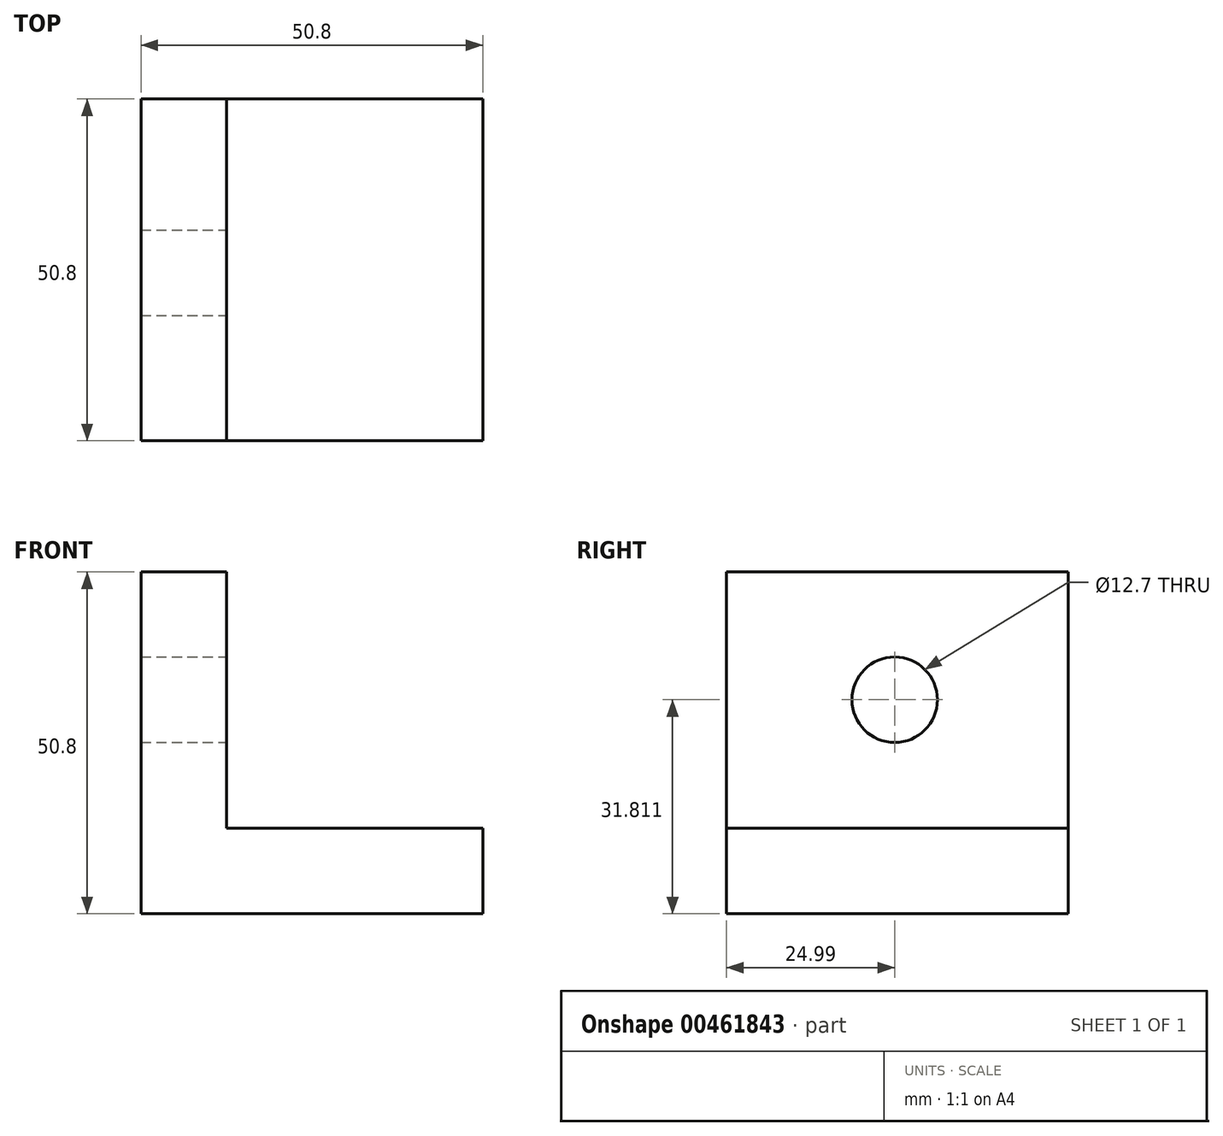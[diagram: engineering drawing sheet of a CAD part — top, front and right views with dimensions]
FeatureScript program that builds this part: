
annotation { "Feature Type Name" : "Feature", "Feature Type Description" : "" }
export const myFeature = defineFeature(function(context is Context, id is Id, definition is map)
    precondition{}
    {
        {
            var Q0;
            Q0=qCreatedBy(makeId("Front.planeOp"),FACE);
            var sketch = newSketch(context, id + "F0", { "sketchPlane" : qUnion([Q0])});
            skLineSegment(sketch, "E0.bottom", {"start": v(-27.84, 30.46) * mm, "end": v(22.96, 30.46) * mm});
            skLineSegment(sketch, "E0.top", {"start": v(-27.84, -20.34) * mm, "end": v(22.96, -20.34) * mm});
            skLineSegment(sketch, "E0.left", {"start": v(-27.84, 30.46) * mm, "end": v(-27.84, -20.34) * mm});
            skLineSegment(sketch, "E0.right", {"start": v(22.96, 30.46) * mm, "end": v(22.96, -20.34) * mm});
            skSolve(sketch);
        }
        {
            var Q0;
            Q0=makeQuery(id+"F0.imprint","IMPRINT",FACE,{"disambiguationData":[TD([[makeQuery(id+"F0.imprint","IMPRINT",EDGE,{"derivedFrom":sQuery(id+"F0.wireOp",EDGE,"E0.bottom")}),-1.0]])]});
            extrude(context, id + "F1", {"entities" : qUnion([Q0]), "depth" : 50.8 * mm});
        }
        {
            var Q0;
            Q0=makeQuery(id+"F1.opExtrude","CAP_FACE",FACE,{"disambiguationData":[OSD([sQuery(id+"F0.wireOp",EDGE,"E0.bottom"),sQuery(id+"F0.wireOp",EDGE,"E0.top"),sQuery(id+"F0.wireOp",EDGE,"E0.left"),sQuery(id+"F0.wireOp",EDGE,"E0.right")])],"isStart":false});
            var sketch = newSketch(context, id + "F2", { "sketchPlane" : qUnion([Q0])});
            skLineSegment(sketch, "E1.bottom", {"start": v(22.96, 30.46) * mm, "end": v(-15.14, 30.46) * mm});
            skLineSegment(sketch, "E1.top", {"start": v(22.96, -7.64) * mm, "end": v(-15.14, -7.64) * mm});
            skLineSegment(sketch, "E1.left", {"start": v(22.96, 30.46) * mm, "end": v(22.96, -7.64) * mm});
            skLineSegment(sketch, "E1.right", {"start": v(-15.14, 30.46) * mm, "end": v(-15.14, -7.64) * mm});
            skSolve(sketch);
        }
        {
            var Q0;
            Q0 = qSketchRegion(id + "F2", true);
            extrude(context, id + "F3", {"entities" : qUnion([Q0]), "operationType" : NewBodyOperationType.REMOVE, "oppositeDirection" : true, "depth" : 61.2 * mm});
        }
        {
            var Q0;
            Q0=makeQuery(id+"F3.boolean.opBoolean","COPY",FACE,{"derivedFrom":makeQuery(id+"F3.opExtrude","SWEPT_FACE",FACE,{"disambiguationData":[OSD([sQuery(id+"F2.wireOp",EDGE,"E1.right")])]})});
            var sketch = newSketch(context, id + "F4", { "sketchPlane" : qUnion([Q0])});
            skCircle(sketch, "E2", {"center": v(-25.8, 11.47) * mm, "radius": 6.35 * mm});
            skSolve(sketch);
        }
        {
            var Q0;
            Q0=makeQuery(id+"F4.imprint","IMPRINT",FACE,{"disambiguationData":[TD([[makeQuery(id+"F4.imprint","IMPRINT",EDGE,{"derivedFrom":sQuery(id+"F4.wireOp",EDGE,"E2")}),1.0]])]});
            var Q1;
            Q1=sQuery(id+"F4.wireOp",EDGE,"E2");
            extrude(context, id + "F5", {"entities" : qUnion([Q0]), "operationType" : NewBodyOperationType.REMOVE, "surfaceEntities" : qUnion([Q1]), "oppositeDirection" : true, "depth" : 35.81 * mm});
        }
    });
